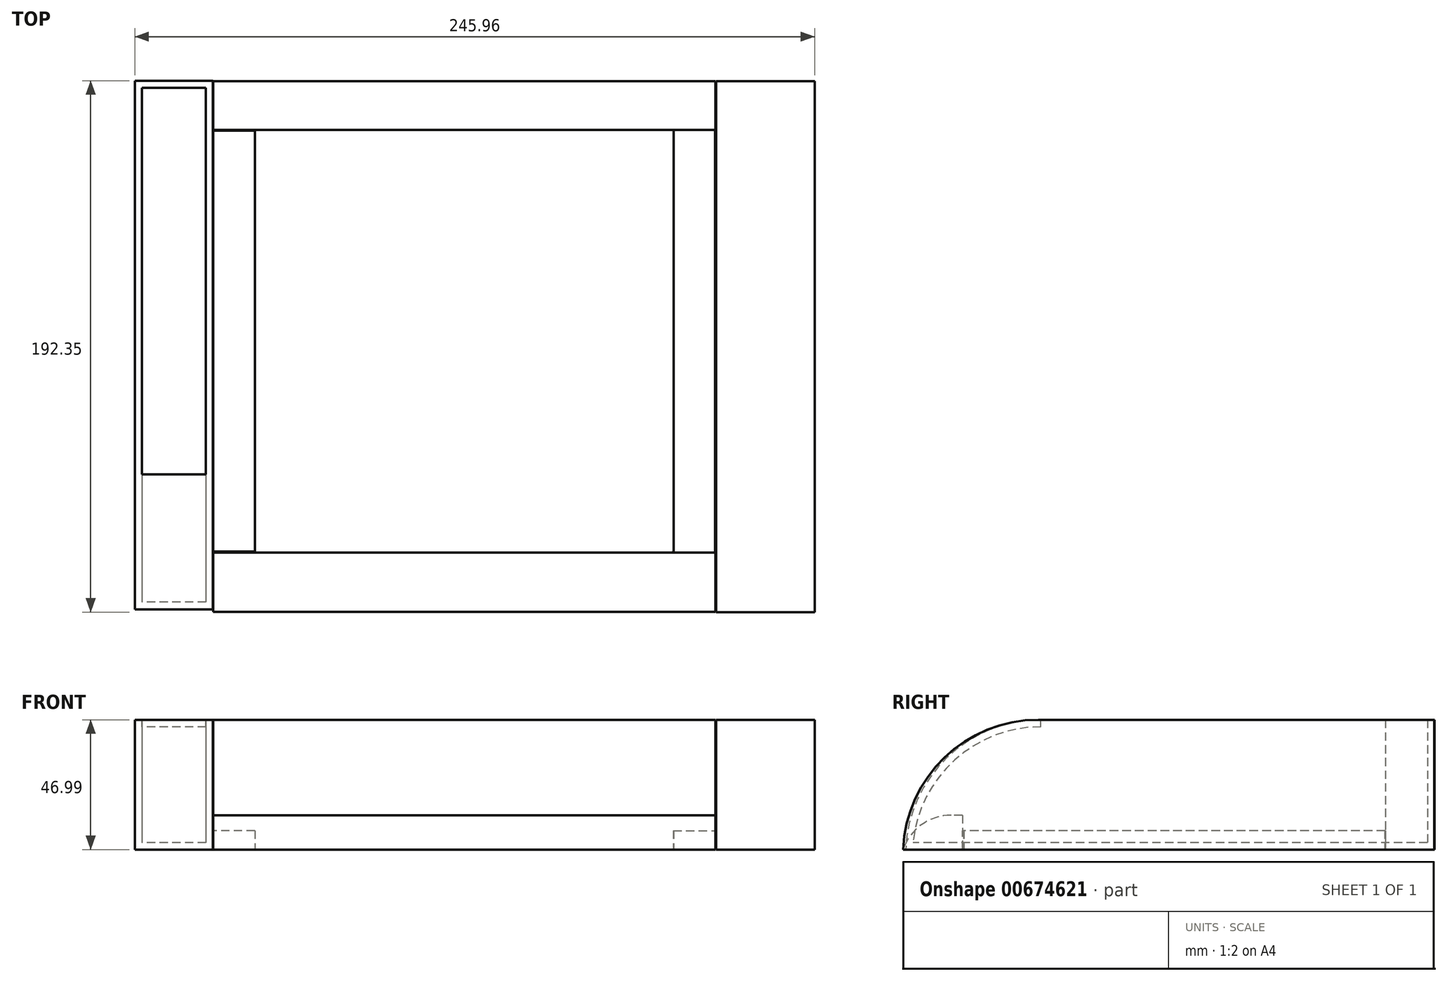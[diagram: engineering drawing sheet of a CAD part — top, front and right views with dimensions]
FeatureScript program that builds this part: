
annotation { "Feature Type Name" : "Feature", "Feature Type Description" : "" }
export const myFeature = defineFeature(function(context is Context, id is Id, definition is map)
    precondition{}
    {
        {
            var Q0;
            Q0=qCreatedBy(makeId("Top.planeOp"),FACE);
            var sketch = newSketch(context, id + "F0", { "sketchPlane" : qUnion([Q0])});
            skLineSegment(sketch, "E0.bottom", {"start": v(-75.78, 76.5) * mm, "end": v(75.78, 76.5) * mm});
            skLineSegment(sketch, "E0.top", {"start": v(-75.78, -75.78) * mm, "end": v(75.78, -75.78) * mm});
            skLineSegment(sketch, "E0.left", {"start": v(-75.78, 76.5) * mm, "end": v(-75.78, -75.78) * mm});
            skLineSegment(sketch, "E0.right", {"start": v(75.78, 76.5) * mm, "end": v(75.78, -75.78) * mm});
            skSolve(sketch);
        }
        {
            var Q0;
            Q0=makeQuery(id+"F0.imprint","IMPRINT",FACE,{"disambiguationData":[TD([[makeQuery(id+"F0.imprint","IMPRINT",EDGE,{"derivedFrom":sQuery(id+"F0.wireOp",EDGE,"E0.bottom")}),-1.0]])]});
            var sketch = newSketch(context, id + "F1", { "sketchPlane" : qUnion([Q0])});
            skLineSegment(sketch, "E1.bottom", {"start": v(-75.77, 76.53) * mm, "end": v(-90.82, 76.53) * mm});
            skLineSegment(sketch, "E1.top", {"start": v(-75.77, -75.89) * mm, "end": v(-90.82, -75.89) * mm});
            skLineSegment(sketch, "E1.left", {"start": v(-75.77, 76.53) * mm, "end": v(-75.77, -75.89) * mm});
            skLineSegment(sketch, "E1.right", {"start": v(-90.82, 76.53) * mm, "end": v(-90.82, -75.89) * mm});
            skLineSegment(sketch, "E2.bottom", {"start": v(75.66, 77.22) * mm, "end": v(90.74, 77.22) * mm});
            skLineSegment(sketch, "E2.top", {"start": v(75.66, -78.63) * mm, "end": v(90.74, -78.63) * mm});
            skLineSegment(sketch, "E2.left", {"start": v(75.66, 77.22) * mm, "end": v(75.66, -78.63) * mm});
            skLineSegment(sketch, "E2.right", {"start": v(90.74, 77.22) * mm, "end": v(90.74, -78.63) * mm});
            skSolve(sketch);
        }
        {
            var Q0;
            {var subQ0=sQuery(id+"F1.wireOp",EDGE,"E1.left");var subQ1=makeQuery(id+"F0.imprint","IMPRINT",EDGE,{"derivedFrom":sQuery(id+"F0.wireOp",EDGE,"E0.bottom")});var subQ2=makeQuery(id+"F1.imprint","INTERSECT",VERTEX,{"derivedFrom":[subQ1,subQ0]});Q0=makeQuery(id+"F1.imprint","IMPRINT",FACE,{"disambiguationData":[TD([[makeQuery(id+"F1.imprint","IMPRINT",EDGE,{"disambiguationData":[TD([[subQ2,-1.0]])],"derivedFrom":subQ0}),1.0]])]});}
            var sketch = newSketch(context, id + "F2", { "sketchPlane" : qUnion([Q0])});
            skLineSegment(sketch, "E3.bottom", {"start": v(-90.78, 76.68) * mm, "end": v(90.9, 76.68) * mm});
            skLineSegment(sketch, "E3.top", {"start": v(-90.78, 94.4) * mm, "end": v(90.9, 94.4) * mm});
            skLineSegment(sketch, "E3.left", {"start": v(-90.78, 76.68) * mm, "end": v(-90.78, 94.4) * mm});
            skLineSegment(sketch, "E3.right", {"start": v(90.9, 76.68) * mm, "end": v(90.9, 94.4) * mm});
            skLineSegment(sketch, "E4.bottom", {"start": v(-90.78, 76.68) * mm, "end": v(-76.9, 76.68) * mm});
            skLineSegment(sketch, "E4.top", {"start": v(-90.78, -76.37) * mm, "end": v(-76.9, -76.37) * mm});
            skLineSegment(sketch, "E4.left", {"start": v(-90.78, 76.68) * mm, "end": v(-90.78, -76.37) * mm});
            skLineSegment(sketch, "E4.right", {"start": v(-76.9, 76.68) * mm, "end": v(-76.9, -76.37) * mm});
            skLineSegment(sketch, "E5.bottom", {"start": v(90.9, 76.68) * mm, "end": v(77.2, 76.68) * mm});
            skLineSegment(sketch, "E5.top", {"start": v(90.9, -76.37) * mm, "end": v(77.2, -76.37) * mm});
            skLineSegment(sketch, "E5.left", {"start": v(90.9, 76.68) * mm, "end": v(90.9, -76.37) * mm});
            skLineSegment(sketch, "E5.right", {"start": v(77.2, 76.68) * mm, "end": v(77.2, -76.37) * mm});
            skSolve(sketch);
        }
        {
            var Q0;
            Q0=makeQuery(id+"F2.imprint","IMPRINT",FACE,{"disambiguationData":[TD([[makeQuery(id+"F2.imprint","IMPRINT",EDGE,{"derivedFrom":sQuery(id+"F2.wireOp",EDGE,"E3.bottom")}),1.0]])]});
            extrude(context, id + "F3", {"entities" : qUnion([Q0]), "depth" : 47 * mm, "offsetDistance" : 25.4 * mm});
        }
        {
            var Q0;
            {var subQ4=sQuery(id+"F1.wireOp",EDGE,"E1.bottom");Q0=makeQuery(id+"F1.imprint","IMPRINT",FACE,{"disambiguationData":[TD([[makeQuery(id+"F1.imprint","IMPRINT",EDGE,{"derivedFrom":subQ4}),1.0]])]});}
            var Q1;
            {var subQ4=sQuery(id+"F1.wireOp",EDGE,"E2.bottom");Q1=makeQuery(id+"F1.imprint","IMPRINT",FACE,{"disambiguationData":[TD([[makeQuery(id+"F1.imprint","IMPRINT",EDGE,{"derivedFrom":subQ4}),-1.0]])]});}
            extrude(context, id + "F4", {"entities" : qUnion([Q0, Q1]), "operationType" : NewBodyOperationType.ADD, "depth" : 6.86 * mm, "offsetDistance" : 25.4 * mm});
        }
        {
            var Q0;
            Q0=makeQuery(id+"F0.imprint","IMPRINT",FACE,{"disambiguationData":[TD([[makeQuery(id+"F0.imprint","IMPRINT",EDGE,{"derivedFrom":sQuery(id+"F0.wireOp",EDGE,"E0.bottom")}),-1.0]])]});
            var sketch = newSketch(context, id + "F5", { "sketchPlane" : qUnion([Q0])});
            skLineSegment(sketch, "E6.bottom", {"start": v(-90.8, -76.31) * mm, "end": v(90.9, -76.31) * mm});
            skLineSegment(sketch, "E6.top", {"start": v(-90.8, -97.83) * mm, "end": v(90.9, -97.83) * mm});
            skLineSegment(sketch, "E6.left", {"start": v(-90.8, -76.31) * mm, "end": v(-90.8, -97.83) * mm});
            skLineSegment(sketch, "E6.right", {"start": v(90.9, -76.31) * mm, "end": v(90.9, -97.83) * mm});
            skSolve(sketch);
        }
        {
            var Q0;
            Q0=makeQuery(id+"F5.imprint","IMPRINT",FACE,{"disambiguationData":[TD([[makeQuery(id+"F5.imprint","IMPRINT",EDGE,{"derivedFrom":sQuery(id+"F5.wireOp",EDGE,"E6.bottom")}),-1.0]])]});
            extrude(context, id + "F6", {"entities" : qUnion([Q0]), "operationType" : NewBodyOperationType.ADD, "depth" : 12.45 * mm, "offsetDistance" : 25.4 * mm});
        }
        {
            var Q0;
            Q0=makeQuery(id+"F0.imprint","IMPRINT",FACE,{"disambiguationData":[TD([[makeQuery(id+"F0.imprint","IMPRINT",EDGE,{"derivedFrom":sQuery(id+"F0.wireOp",EDGE,"E0.bottom")}),-1.0]])]});
            var sketch = newSketch(context, id + "F7", { "sketchPlane" : qUnion([Q0])});
            skLineSegment(sketch, "E7.bottom", {"start": v(-90.9, 94.5) * mm, "end": v(-119.17, 94.5) * mm});
            skLineSegment(sketch, "E7.top", {"start": v(-90.9, -96.94) * mm, "end": v(-119.17, -96.94) * mm});
            skLineSegment(sketch, "E7.left", {"start": v(-90.9, 94.5) * mm, "end": v(-90.9, -96.94) * mm});
            skLineSegment(sketch, "E7.right", {"start": v(-119.17, 94.5) * mm, "end": v(-119.17, -96.94) * mm});
            skLineSegment(sketch, "E8.bottom", {"start": v(90.91, -96.96) * mm, "end": v(118.47, -96.96) * mm});
            skLineSegment(sketch, "E8.top", {"start": v(90.91, 94.12) * mm, "end": v(118.47, 94.12) * mm});
            skLineSegment(sketch, "E8.left", {"start": v(90.91, -96.96) * mm, "end": v(90.91, 94.12) * mm});
            skLineSegment(sketch, "E8.right", {"start": v(118.47, -96.96) * mm, "end": v(118.47, 94.12) * mm});
            skSolve(sketch);
        }
        {
            var Q0;
            Q0=makeQuery(id+"F7.imprint","IMPRINT",FACE,{"disambiguationData":[TD([[makeQuery(id+"F7.imprint","IMPRINT",EDGE,{"derivedFrom":sQuery(id+"F7.wireOp",EDGE,"E7.bottom")}),1.0]])]});
            extrude(context, id + "F8", {"entities" : qUnion([Q0]), "depth" : 47 * mm, "offsetDistance" : 25.4 * mm});
        }
        {
            var Q0;
            Q0=makeQuery(id+"F0.imprint","IMPRINT",FACE,{"disambiguationData":[TD([[makeQuery(id+"F0.imprint","IMPRINT",EDGE,{"derivedFrom":sQuery(id+"F0.wireOp",EDGE,"E0.bottom")}),-1.0]])]});
            var sketch = newSketch(context, id + "F9", { "sketchPlane" : qUnion([Q0])});
            skLineSegment(sketch, "E9.bottom", {"start": v(91.1, 94.39) * mm, "end": v(126.8, 94.39) * mm});
            skLineSegment(sketch, "E9.top", {"start": v(91.1, -97.84) * mm, "end": v(126.8, -97.84) * mm});
            skLineSegment(sketch, "E9.left", {"start": v(91.1, 94.39) * mm, "end": v(91.1, -97.84) * mm});
            skLineSegment(sketch, "E9.right", {"start": v(126.8, 94.39) * mm, "end": v(126.8, -97.84) * mm});
            skSolve(sketch);
        }
        {
            var Q0;
            Q0=makeQuery(id+"F9.imprint","IMPRINT",FACE,{"disambiguationData":[TD([[makeQuery(id+"F9.imprint","IMPRINT",EDGE,{"derivedFrom":sQuery(id+"F9.wireOp",EDGE,"E9.bottom")}),-1.0]])]});
            extrude(context, id + "F10", {"entities" : qUnion([Q0]), "depth" : 47 * mm, "offsetDistance" : 25.4 * mm});
        }
        {
            var Q0;
            Q0=makeQuery(id+"F8.opExtrude","CAP_EDGE",EDGE,{"disambiguationData":[OSD([sQuery(id+"F7.wireOp",EDGE,"E7.top")])],"isStart":false});
            var Q1;
            Q1=makeQuery(id+"F10.opExtrude","CAP_EDGE",EDGE,{"disambiguationData":[OSD([sQuery(id+"F9.wireOp",EDGE,"E9.top")])],"isStart":false});
            fillet(context, id + "F11", {"entities" : qUnion([Q0, Q1]), "radius" : 49.06 * mm, "tangentPropagation" : true, "allowEdgeOverflow" : false});
        }
        {
            var Q0;
            Q0=makeQuery(id+"F6.opExtrude","CAP_EDGE",EDGE,{"disambiguationData":[OSD([sQuery(id+"F5.wireOp",EDGE,"E6.top")])],"isStart":false});
            fillet(context, id + "F12", {"entities" : qUnion([Q0]), "radius" : 18.4 * mm, "tangentPropagation" : true, "allowEdgeOverflow" : false});
        }
        {
            var Q0;
            Q0=makeQuery(id+"F8.opExtrude","CAP_FACE",FACE,{"disambiguationData":[OSD([sQuery(id+"F7.wireOp",EDGE,"E7.bottom"),sQuery(id+"F7.wireOp",EDGE,"E7.top"),sQuery(id+"F7.wireOp",EDGE,"E7.left"),sQuery(id+"F7.wireOp",EDGE,"E7.right")])],"isStart":false});
            shell(context, id + "F13", {"entities" : qUnion([Q0]), "thickness" : 2.54 * mm});
        }
    });
